# Revit family: Charlottesville w Brass 30 Vanity - Vintage Black
name_source: partatom
category: Casework
units: mm (PartAtom-declared; Revit-internal decimal feet)

## family parameters
Always vertical = Yes
Cut with Voids When Loaded = No
Host = Wall
OmniClass Number = 23.40.35.00
OmniClass Title = Casework
Room Calculation Point = No
Shared = No

## types (1)
- Charlottesville w Brass 30 Vanity - Vintage Black
    Area = 0
    BarCode = <None>
    Default Elevation = 2' - 4"
    Depth = 1' - 9 1/2"
    HandicapAccessible = Yes
    Height = 0' - 9"
    Height of Cabinet = 2' - 1"
    Height of Countertop = 0' - 1"
    IsExtendedWarranty = 0
    Length = 4' - 0"
    NominalHeight = 0
    NominalLength = 0
    NominalWidth = 0
    ReplacementCost = 0
    SelfClosing = Yes
    WarrantyDurationLabor = 0
    WarrantyDurationParts = 0
    WarrantyPeriod = 0
    Width = 2' - 6"

## geometry (parser evidence)
native form markers: Blend x6, Sweep x8
no freeform markers — native parametric forms only
